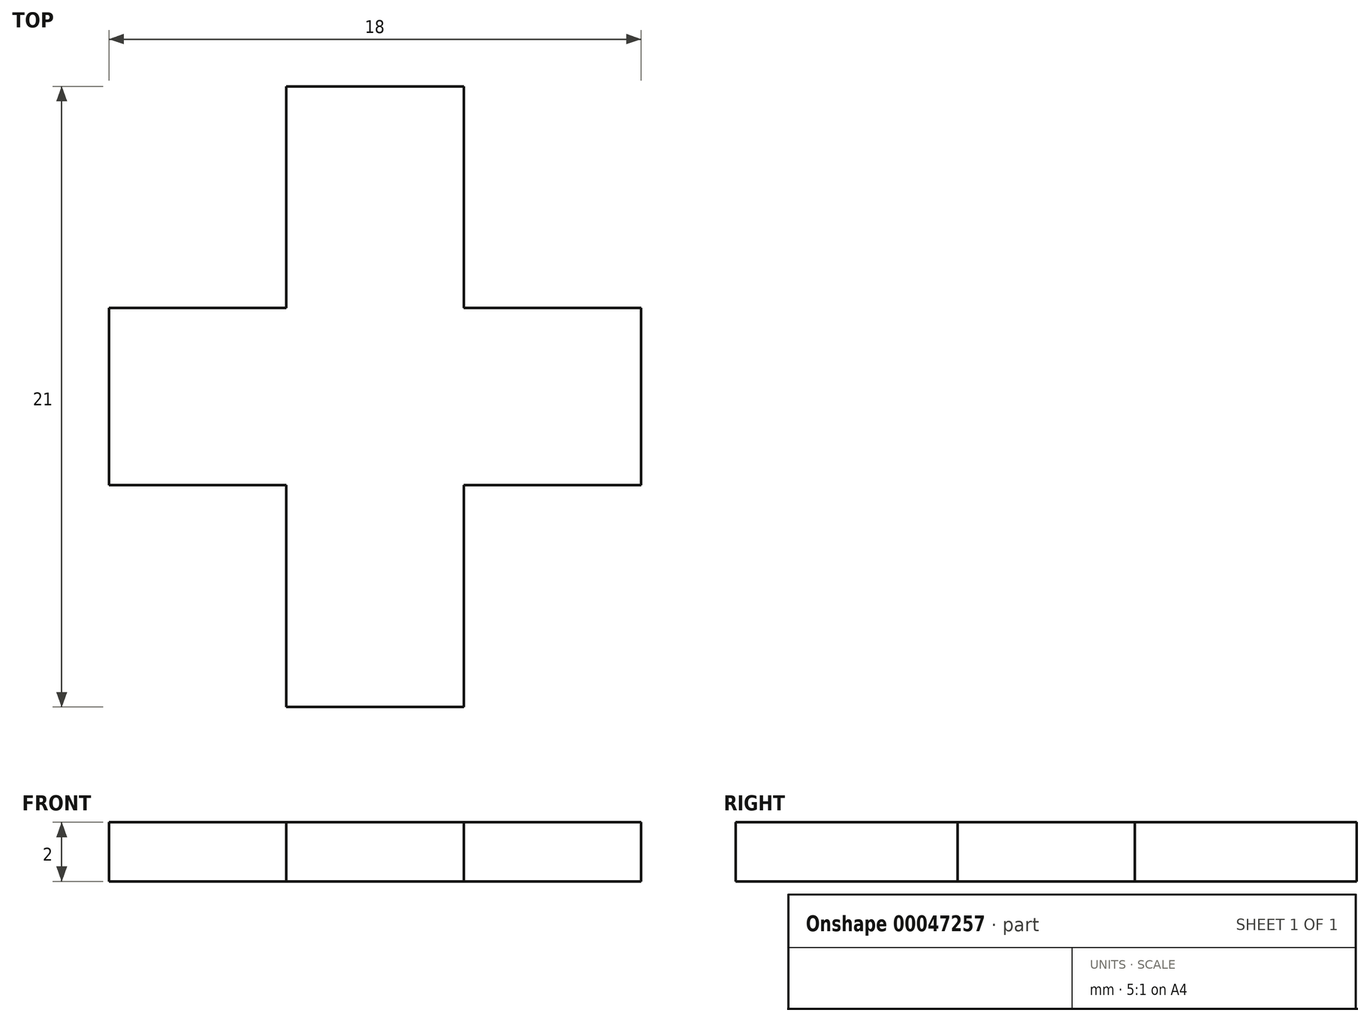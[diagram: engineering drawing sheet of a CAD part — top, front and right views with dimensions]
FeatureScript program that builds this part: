
annotation { "Feature Type Name" : "Feature", "Feature Type Description" : "" }
export const myFeature = defineFeature(function(context is Context, id is Id, definition is map)
    precondition{}
    {
        {
            var Q0;
            Q0=qCreatedBy(makeId("Top.planeOp"),FACE);
            var sketch = newSketch(context, id + "F0", { "sketchPlane" : qUnion([Q0])});
            skLineSegment(sketch, "E0", {"start": v(0, 0) * mm, "end": v(9, 0) * mm});
            skLineSegment(sketch, "E1", {"start": v(9, 3) * mm, "end": v(3, 3) * mm});
            skLineSegment(sketch, "E2", {"start": v(3, 3) * mm, "end": v(3, 10.5) * mm});
            skLineSegment(sketch, "E3", {"start": v(3, 10.5) * mm, "end": v(-3, 10.5) * mm});
            skLineSegment(sketch, "E4", {"start": v(-3, 10.5) * mm, "end": v(-3, 3) * mm});
            skLineSegment(sketch, "E5", {"start": v(-3, 3) * mm, "end": v(-9, 3) * mm});
            skLineSegment(sketch, "E6", {"start": v(-9, 3) * mm, "end": v(-9, -3) * mm});
            skLineSegment(sketch, "E7", {"start": v(-9, -3) * mm, "end": v(-3, -3) * mm});
            skLineSegment(sketch, "E8", {"start": v(-3, -3) * mm, "end": v(-3, -10.5) * mm});
            skLineSegment(sketch, "E9", {"start": v(-3, -10.5) * mm, "end": v(3, -10.5) * mm});
            skLineSegment(sketch, "E10", {"start": v(3, -10.5) * mm, "end": v(3, -3) * mm});
            skLineSegment(sketch, "E11", {"start": v(3, -3) * mm, "end": v(9, -3) * mm});
            skLineSegment(sketch, "E12", {"start": v(9, -3) * mm, "end": v(9, 3) * mm});
            skLineSegment(sketch, "E13", {"start": v(-3, -3) * mm, "end": v(0, 0) * mm, "construction": true});
            skLineSegment(sketch, "E14", {"start": v(0, 0) * mm, "end": v(3, -3) * mm, "construction": true});
            skSolve(sketch);
        }
        {
            var Q0;
            Q0 = qSketchRegion(id + "F0", true);
            extrude(context, id + "F1", {"entities" : qUnion([Q0]), "depth" : 2 * mm});
        }
    });
